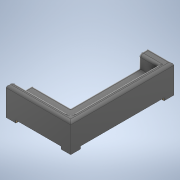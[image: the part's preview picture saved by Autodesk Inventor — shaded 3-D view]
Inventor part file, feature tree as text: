
AUTODESK INVENTOR PART (.ipt)
format: ipt  version: 2022 (Build 260153000, 153)  size: 219,136 bytes
history: native  units: mm
features: extrude x4, sketch x3, fillet x1
ambient origin geometry x8: Origin, YZ Plane, XZ Plane, XY Plane, X Axis, Y Axis, Z Axis, Center Point
bodies: Solid1 (feature_tree)
feature tree (8):
  extrude  "Extrusion1"  Depth=20.0mm
  sketch  "Sketch3"  dims[d2=80.0mm d3=20.0mm]
  extrude  "Extrusion2"  Depth=20.0mm
  extrude  "Extrusion3"  TaperAngle=0.0deg  [1 undecoded]
  fillet  "Fillet1"  Radius=10.0mm
  extrude  "Extrusion4"  Depth=20.0mm
  sketch  "Sketch1"  dims[d0=50.0mm d1=20.0mm]
  sketch  "Sketch4"  dims[d4=0.0mm d5=0.0mm d6=10.0mm d7=0.0mm d8=20.0mm d9=7.5mm d10=5.0mm d11=80.0mm d12=10.0mm d13=0.0mm d14=50.0mm d15=5.0mm d16=10.0mm d17=0.0mm d18=2.0mm d19=7.5mm d20=7.5mm d21=7.5mm d22=7.5mm d23=7.5mm d24=7.5mm d25=7.7mm d26=7.5mm d27=7.5mm d28=7.5mm d29=7.5mm d30=7.5mm d31=2.0mm d32=0.0mm d33=0.0mm d34=0.0mm d35=0.0mm d36=0.0mm]
note: 1 required parameter value undecoded (feature->parameter linkage not recoverable at this tier; creation-order binding heuristic only, values carry confidence <= 0.55)
